FCSTD DOCUMENT  (FreeCAD 1.0R39109 (Git))
Label: female connector mk2
License: All rights reserved
LicenseURL: http://en.wikipedia.org/wiki/All_rights_reserved
objects: Sketcher::SketchObject×1, PartDesign::Body×1
note: 3 computed .brp shape members not serialized (recipe doc carries the construction recipe); baked Part::Feature solids carry a one-line shape summary decoded from their .brp

FEATURE [Sketcher::SketchObject] Sketch
  ArcFitTolerance = 0
  AttachmentSupport = -> [XY_Plane]
  FullyConstrained = true
  MakeInternals = false
  MapMode = 5
  sketch-geometry (4):
    g0: ArcOfCircle CenterX=0 CenterY=0 CenterZ=0 NormalX=0 NormalY=0 NormalZ=1 AngleXU=0 Radius=7 StartAngle=2.26902 EndAngle=7.15576
    g1: LineSegment StartX=-4.5 StartY=5.3619 StartZ=0 EndX=-4.5 EndY=12.3619 EndZ=0
    g2: LineSegment StartX=-4.5 StartY=12.3619 StartZ=0 EndX=4.5 EndY=12.3619 EndZ=0
    g3: LineSegment StartX=4.5 StartY=12.3619 StartZ=0 EndX=4.5 EndY=5.3619 EndZ=0
  constraints (12):
    c: Coincident(g0,g-1)
    c: Vertical(g1)
    c: Coincident(g2,g1)
    c: Coincident(g3,g2)
    c: Vertical(g3)
    c: Horizontal(g2)
    c: Equal(g1,g3)
    c: Diameter(g0) = 14
    c: DistanceY(g1,g1) = 7
    c: DistanceX(g2,g2) = 9
    c: Coincident(g0,g1)
    c: Coincident(g0,g3)
FEATURE [PartDesign::Body] Body
  AllowCompound = false
  Group = -> [Sketch]
  Origin = -> Origin
